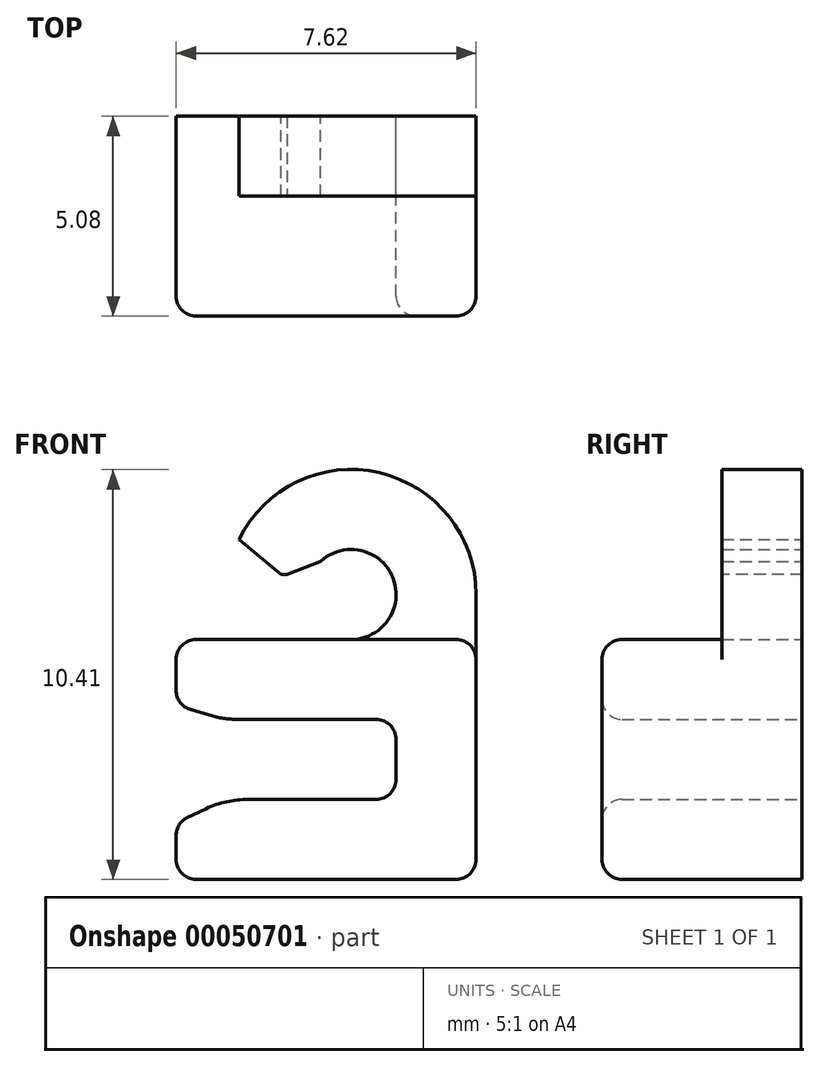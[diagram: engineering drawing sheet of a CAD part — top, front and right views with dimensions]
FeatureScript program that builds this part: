
annotation { "Feature Type Name" : "Feature", "Feature Type Description" : "" }
export const myFeature = defineFeature(function(context is Context, id is Id, definition is map)
    precondition{}
    {
        {
            var Q0;
            Q0=qCreatedBy(makeId("Front.planeOp"),FACE);
            var sketch = newSketch(context, id + "F0", { "sketchPlane" : qUnion([Q0])});
            skLineSegment(sketch, "E0", {"start": v(0, 0) * mm, "end": v(-7.62, 0) * mm});
            skLineSegment(sketch, "E1", {"start": v(-7.62, 0) * mm, "end": v(-7.62, 2.03) * mm});
            skLineSegment(sketch, "E2", {"start": v(-7.62, 2.03) * mm, "end": v(-2.03, 2.03) * mm});
            skLineSegment(sketch, "E3", {"start": v(-2.03, 2.03) * mm, "end": v(-2.03, 4.06) * mm});
            skLineSegment(sketch, "E4", {"start": v(-2.03, 4.06) * mm, "end": v(-7.62, 4.06) * mm});
            skLineSegment(sketch, "E5", {"start": v(-7.62, 4.06) * mm, "end": v(-7.62, 6.1) * mm});
            skLineSegment(sketch, "E6", {"start": v(-7.62, 6.1) * mm, "end": v(-3.18, 6.1) * mm});
            skLineSegment(sketch, "E7", {"start": v(0, 0) * mm, "end": v(0, 7.24) * mm});
            skArc(sketch, "E8", {"start": v(-3.18, 6.1) * mm, "mid": v(-2.2, 7.84) * mm, "end": v(-4.2, 7.75) * mm});
            skArc(sketch, "E9", {"start": v(0, 7.24) * mm, "mid": v(-2.92, 10.4) * mm, "end": v(-6.3, 7.75) * mm});
            skLineSegment(sketch, "E10", {"start": v(-4.2, 7.75) * mm, "end": v(-6.3, 7.75) * mm});
            skPoint(sketch, "E11.end.orphan", {"position": v(-2.03, 7.24) * mm});
            skSolve(sketch);
        }
        {
            var Q0;
            Q0 = qSketchRegion(id + "F0", true);
            extrude(context, id + "F1", {"entities" : qUnion([Q0]), "depth" : 2.03 * mm});
        }
        {
            var Q0;
            Q0=makeQuery(id+"F1.opExtrude","CAP_FACE",FACE,{"disambiguationData":[OSD([sQuery(id+"F0.wireOp",EDGE,"E0"),sQuery(id+"F0.wireOp",EDGE,"E1"),sQuery(id+"F0.wireOp",EDGE,"E2"),sQuery(id+"F0.wireOp",EDGE,"E3"),sQuery(id+"F0.wireOp",EDGE,"E4"),sQuery(id+"F0.wireOp",EDGE,"E5"),sQuery(id+"F0.wireOp",EDGE,"E6"),sQuery(id+"F0.wireOp",EDGE,"E7"),sQuery(id+"F0.wireOp",EDGE,"E8"),sQuery(id+"F0.wireOp",EDGE,"E9"),sQuery(id+"F0.wireOp",EDGE,"E10")])],"isStart":false});
            var sketch = newSketch(context, id + "F2", { "sketchPlane" : qUnion([Q0])});
            skLineSegment(sketch, "E12.0", {"start": v(-7.62, 6.1) * mm, "end": v(0, 6.1) * mm});
            skLineSegment(sketch, "E13.0", {"start": v(0, 0) * mm, "end": v(0, 7.24) * mm});
            skPoint(sketch, "E14.orphan", {"position": v(-3.18, 6.1) * mm});
            skSolve(sketch);
        }
        {
            var Q0;
            Q0 = qSketchRegion(id + "F2", true);
            var Q1;
            {var subQ0=makeQuery(id+"F1.opExtrude","CAP_EDGE",EDGE,{"disambiguationData":[OSD([sQuery(id+"F0.wireOp",EDGE,"E0")])],"isStart":false});Q1=makeQuery(id+"F2.imprint","IMPRINT",FACE,{"disambiguationData":[TD([[makeQuery(id+"F2.imprint","IMPRINT",EDGE,{"derivedFrom":subQ0}),-1.0]])]});}
            extrude(context, id + "F3", {"entities" : qUnion([Q0, Q1]), "operationType" : NewBodyOperationType.ADD, "depth" : 3.05 * mm});
        }
        {
            var Q0;
            Q0=makeQuery(id+"F1.opExtrude","SWEPT_EDGE",EDGE,{"disambiguationData":[OSD([sQuery(id+"F0.wireOp",EDGE,"E9"),sQuery(id+"F0.wireOp",EDGE,"E10")])]});
            var Q1;
            {var subQ0=sQuery(id+"F0.wireOp",EDGE,"E5");var subQ1=sQuery(id+"F0.wireOp",EDGE,"E4");Q1=makeQuery(id+"F3.boolean.opBoolean","MERGE",EDGE,{"derivedFrom":[makeQuery(id+"F1.opExtrude","SWEPT_EDGE",EDGE,{"disambiguationData":[OSD([subQ1,subQ0])]}),makeQuery(id+"F3.opExtrude","SWEPT_EDGE",EDGE,{"disambiguationData":[OSD([subQ1,subQ0])]})]});}
            chamfer(context, id + "F4", {"entities" : qUnion([Q0, Q1]), "chamferType" : ChamferType.OFFSET_ANGLE, "width" : 1.27 * mm, "oppositeDirection" : false, "angle" : 25 * degree, "tangentPropagation" : true});
        }
        {
            var Q0;
            {var subQ0=sQuery(id+"F0.wireOp",EDGE,"E2");var subQ1=sQuery(id+"F0.wireOp",EDGE,"E1");Q0=makeQuery(id+"F3.boolean.opBoolean","MERGE",EDGE,{"derivedFrom":[makeQuery(id+"F1.opExtrude","SWEPT_EDGE",EDGE,{"disambiguationData":[OSD([subQ1,subQ0])]}),makeQuery(id+"F3.opExtrude","SWEPT_EDGE",EDGE,{"disambiguationData":[OSD([subQ1,subQ0])]})]});}
            chamfer(context, id + "F5", {"entities" : qUnion([Q0]), "chamferType" : ChamferType.OFFSET_ANGLE, "width" : 1.27 * mm, "oppositeDirection" : true, "angle" : 25 * degree, "tangentPropagation" : true});
        }
        {
            var Q0;
            Q0=makeQuery(id+"F1.opExtrude","SWEPT_EDGE",EDGE,{"disambiguationData":[OSD([sQuery(id+"F0.wireOp",EDGE,"E8"),sQuery(id+"F0.wireOp",EDGE,"E10")])]});
            chamfer(context, id + "F6", {"entities" : qUnion([Q0]), "width" : 1.27 * mm, "tangentPropagation" : true});
        }
        {
            var Q0;
            Q0=makeQuery(id+"F3.opExtrude","CAP_EDGE",EDGE,{"disambiguationData":[OSD([sQuery(id+"F2.wireOp",EDGE,"E12.0")])],"isStart":true});
            var Q1;
            {var subQ0=sQuery(id+"F0.wireOp",EDGE,"E4");var subQ1=sQuery(id+"F0.wireOp",EDGE,"E5");Q1=makeQuery(id+"F4.opChamfer","BLEND_EDGE",EDGE,{"blendedFrom":[makeQuery(id+"F3.boolean.opBoolean","MERGE",EDGE,{"derivedFrom":[makeQuery(id+"F1.opExtrude","SWEPT_EDGE",EDGE,{"disambiguationData":[OSD([subQ0,subQ1])]}),makeQuery(id+"F3.opExtrude","SWEPT_EDGE",EDGE,{"disambiguationData":[OSD([subQ0,subQ1])]})]}),makeQuery(id+"F3.boolean.opBoolean","MERGE",FACE,{"derivedFrom":[makeQuery(id+"F1.opExtrude","SWEPT_FACE",FACE,{"disambiguationData":[OSD([subQ0])]}),makeQuery(id+"F3.opExtrude","SWEPT_FACE",FACE,{"disambiguationData":[OSD([subQ0])]})]})],"blendedInto":[makeQuery(id+"F3.boolean.opBoolean","MERGE",FACE,{"derivedFrom":[makeQuery(id+"F1.opExtrude","SWEPT_FACE",FACE,{"disambiguationData":[OSD([subQ0])]}),makeQuery(id+"F3.opExtrude","SWEPT_FACE",FACE,{"disambiguationData":[OSD([subQ0])]})]})]});}
            var Q2;
            {var subQ0=sQuery(id+"F0.wireOp",EDGE,"E2");var subQ1=sQuery(id+"F0.wireOp",EDGE,"E1");Q2=makeQuery(id+"F5.opChamfer","BLEND_EDGE",EDGE,{"blendedFrom":[makeQuery(id+"F3.boolean.opBoolean","MERGE",EDGE,{"derivedFrom":[makeQuery(id+"F1.opExtrude","SWEPT_EDGE",EDGE,{"disambiguationData":[OSD([subQ1,subQ0])]}),makeQuery(id+"F3.opExtrude","SWEPT_EDGE",EDGE,{"disambiguationData":[OSD([subQ1,subQ0])]})]}),makeQuery(id+"F3.boolean.opBoolean","MERGE",FACE,{"derivedFrom":[makeQuery(id+"F1.opExtrude","SWEPT_FACE",FACE,{"disambiguationData":[OSD([subQ0])]}),makeQuery(id+"F3.opExtrude","SWEPT_FACE",FACE,{"disambiguationData":[OSD([subQ0])]})]})],"blendedInto":[makeQuery(id+"F3.boolean.opBoolean","MERGE",FACE,{"derivedFrom":[makeQuery(id+"F1.opExtrude","SWEPT_FACE",FACE,{"disambiguationData":[OSD([subQ0])]}),makeQuery(id+"F3.opExtrude","SWEPT_FACE",FACE,{"disambiguationData":[OSD([subQ0])]})]})]});}
            fillet(context, id + "F7", {"entities" : qUnion([Q0, Q1, Q2]), "radius" : 2.54 * mm, "tangentPropagation" : true, "allowEdgeOverflow" : false});
        }
        {
            var Q0;
            Q0=makeQuery(id+"F3.opExtrude","SWEPT_EDGE",EDGE,{"disambiguationData":[OSD([sQuery(id+"F2.wireOp",EDGE,"E12.0"),sQuery(id+"F2.wireOp",EDGE,"E13.0")])]});
            var Q1;
            {var subQ0=sQuery(id+"F0.wireOp",EDGE,"E0");Q1=makeQuery(id+"F3.boolean.opBoolean","MERGE",EDGE,{"derivedFrom":[makeQuery(id+"F1.opExtrude","SWEPT_EDGE",EDGE,{"disambiguationData":[OSD([subQ0,sQuery(id+"F0.wireOp",EDGE,"E7")])]}),makeQuery(id+"F3.opExtrude","SWEPT_EDGE",EDGE,{"disambiguationData":[OSD([subQ0,sQuery(id+"F2.wireOp",EDGE,"E13.0")])]})]});}
            var Q2;
            {var subQ0=sQuery(id+"F0.wireOp",EDGE,"E1");var subQ1=sQuery(id+"F0.wireOp",EDGE,"E2");Q2=makeQuery(id+"F5.opChamfer","BLEND_EDGE",EDGE,{"blendedFrom":[makeQuery(id+"F3.boolean.opBoolean","MERGE",EDGE,{"derivedFrom":[makeQuery(id+"F1.opExtrude","SWEPT_EDGE",EDGE,{"disambiguationData":[OSD([subQ0,subQ1])]}),makeQuery(id+"F3.opExtrude","SWEPT_EDGE",EDGE,{"disambiguationData":[OSD([subQ0,subQ1])]})]}),makeQuery(id+"F3.boolean.opBoolean","MERGE",FACE,{"derivedFrom":[makeQuery(id+"F1.opExtrude","SWEPT_FACE",FACE,{"disambiguationData":[OSD([subQ0])]}),makeQuery(id+"F3.opExtrude","SWEPT_FACE",FACE,{"disambiguationData":[OSD([subQ0])]})]})],"blendedInto":[makeQuery(id+"F3.boolean.opBoolean","MERGE",FACE,{"derivedFrom":[makeQuery(id+"F1.opExtrude","SWEPT_FACE",FACE,{"disambiguationData":[OSD([subQ0])]}),makeQuery(id+"F3.opExtrude","SWEPT_FACE",FACE,{"disambiguationData":[OSD([subQ0])]})]})]});}
            var Q3;
            {var subQ0=sQuery(id+"F0.wireOp",EDGE,"E5");var subQ1=sQuery(id+"F0.wireOp",EDGE,"E4");Q3=makeQuery(id+"F4.opChamfer","BLEND_EDGE",EDGE,{"blendedFrom":[makeQuery(id+"F3.boolean.opBoolean","MERGE",EDGE,{"derivedFrom":[makeQuery(id+"F1.opExtrude","SWEPT_EDGE",EDGE,{"disambiguationData":[OSD([subQ1,subQ0])]}),makeQuery(id+"F3.opExtrude","SWEPT_EDGE",EDGE,{"disambiguationData":[OSD([subQ1,subQ0])]})]}),makeQuery(id+"F3.boolean.opBoolean","MERGE",FACE,{"derivedFrom":[makeQuery(id+"F1.opExtrude","SWEPT_FACE",FACE,{"disambiguationData":[OSD([subQ0])]}),makeQuery(id+"F3.opExtrude","SWEPT_FACE",FACE,{"disambiguationData":[OSD([subQ0])]})]})],"blendedInto":[makeQuery(id+"F3.boolean.opBoolean","MERGE",FACE,{"derivedFrom":[makeQuery(id+"F1.opExtrude","SWEPT_FACE",FACE,{"disambiguationData":[OSD([subQ0])]}),makeQuery(id+"F3.opExtrude","SWEPT_FACE",FACE,{"disambiguationData":[OSD([subQ0])]})]})]});}
            var Q4;
            Q4=makeQuery(id+"F7.opFillet","BLEND_EDGE",EDGE,{"blendedFrom":[makeQuery(id+"F3.opExtrude","CAP_EDGE",EDGE,{"disambiguationData":[OSD([sQuery(id+"F2.wireOp",EDGE,"E12.0")])],"isStart":true}),makeQuery(id+"F1.opExtrude","SWEPT_FACE",FACE,{"disambiguationData":[OSD([sQuery(id+"F0.wireOp",EDGE,"E8")])]})],"blendedInto":[makeQuery(id+"F1.opExtrude","SWEPT_FACE",FACE,{"disambiguationData":[OSD([sQuery(id+"F0.wireOp",EDGE,"E8")])]})]});
            var Q5;
            {var subQ0=sQuery(id+"F0.wireOp",EDGE,"E4");var subQ1=sQuery(id+"F0.wireOp",EDGE,"E3");Q5=makeQuery(id+"F3.boolean.opBoolean","MERGE",EDGE,{"derivedFrom":[makeQuery(id+"F1.opExtrude","SWEPT_EDGE",EDGE,{"disambiguationData":[OSD([subQ1,subQ0])]}),makeQuery(id+"F3.opExtrude","SWEPT_EDGE",EDGE,{"disambiguationData":[OSD([subQ1,subQ0])]})]});}
            var Q6;
            {var subQ0=sQuery(id+"F0.wireOp",EDGE,"E3");var subQ1=sQuery(id+"F0.wireOp",EDGE,"E2");Q6=makeQuery(id+"F3.boolean.opBoolean","MERGE",EDGE,{"derivedFrom":[makeQuery(id+"F1.opExtrude","SWEPT_EDGE",EDGE,{"disambiguationData":[OSD([subQ1,subQ0])]}),makeQuery(id+"F3.opExtrude","SWEPT_EDGE",EDGE,{"disambiguationData":[OSD([subQ1,subQ0])]})]});}
            fillet(context, id + "F8", {"entities" : qUnion([Q0, Q1, Q2, Q3, Q4, Q5, Q6]), "radius" : 0.5 * mm, "tangentPropagation" : true, "allowEdgeOverflow" : false});
        }
        {
            var Q0;
            {var subQ0=sQuery(id+"F0.wireOp",EDGE,"E10");Q0=makeQuery(id+"F6.opChamfer","BLEND_EDGE",EDGE,{"blendedFrom":[makeQuery(id+"F1.opExtrude","SWEPT_EDGE",EDGE,{"disambiguationData":[OSD([sQuery(id+"F0.wireOp",EDGE,"E8"),subQ0])]}),makeQuery(id+"F4.opChamfer","BLEND_FACE",FACE,{"disambiguationData":[OSD([sQuery(id+"F0.wireOp",EDGE,"E9"),subQ0])]})],"blendedInto":[makeQuery(id+"F4.opChamfer","BLEND_FACE",FACE,{"disambiguationData":[OSD([sQuery(id+"F0.wireOp",EDGE,"E9"),subQ0])]})]});}
            var Q1;
            {var subQ0=sQuery(id+"F0.wireOp",EDGE,"E5");Q1=makeQuery(id+"F3.boolean.opBoolean","MERGE",EDGE,{"derivedFrom":[makeQuery(id+"F1.opExtrude","SWEPT_EDGE",EDGE,{"disambiguationData":[OSD([subQ0,sQuery(id+"F0.wireOp",EDGE,"E6")])]}),makeQuery(id+"F3.opExtrude","SWEPT_EDGE",EDGE,{"disambiguationData":[OSD([subQ0,sQuery(id+"F2.wireOp",EDGE,"E12.0")])]})]});}
            var Q2;
            {var subQ0=sQuery(id+"F0.wireOp",EDGE,"E1");var subQ1=sQuery(id+"F0.wireOp",EDGE,"E0");Q2=makeQuery(id+"F3.boolean.opBoolean","MERGE",EDGE,{"derivedFrom":[makeQuery(id+"F1.opExtrude","SWEPT_EDGE",EDGE,{"disambiguationData":[OSD([subQ1,subQ0])]}),makeQuery(id+"F3.opExtrude","SWEPT_EDGE",EDGE,{"disambiguationData":[OSD([subQ1,subQ0])]})]});}
            var Q3;
            Q3=makeQuery(id+"F3.opExtrude","CAP_EDGE",EDGE,{"disambiguationData":[OSD([sQuery(id+"F0.wireOp",EDGE,"E0")])],"isStart":false});
            var Q4;
            Q4=makeQuery(id+"F3.opExtrude","CAP_EDGE",EDGE,{"disambiguationData":[OSD([sQuery(id+"F0.wireOp",EDGE,"E1")])],"isStart":false});
            fillet(context, id + "F9", {"entities" : qUnion([Q0, Q1, Q2, Q3, Q4]), "radius" : 0.5 * mm, "tangentPropagation" : true, "allowEdgeOverflow" : false});
        }
    });
